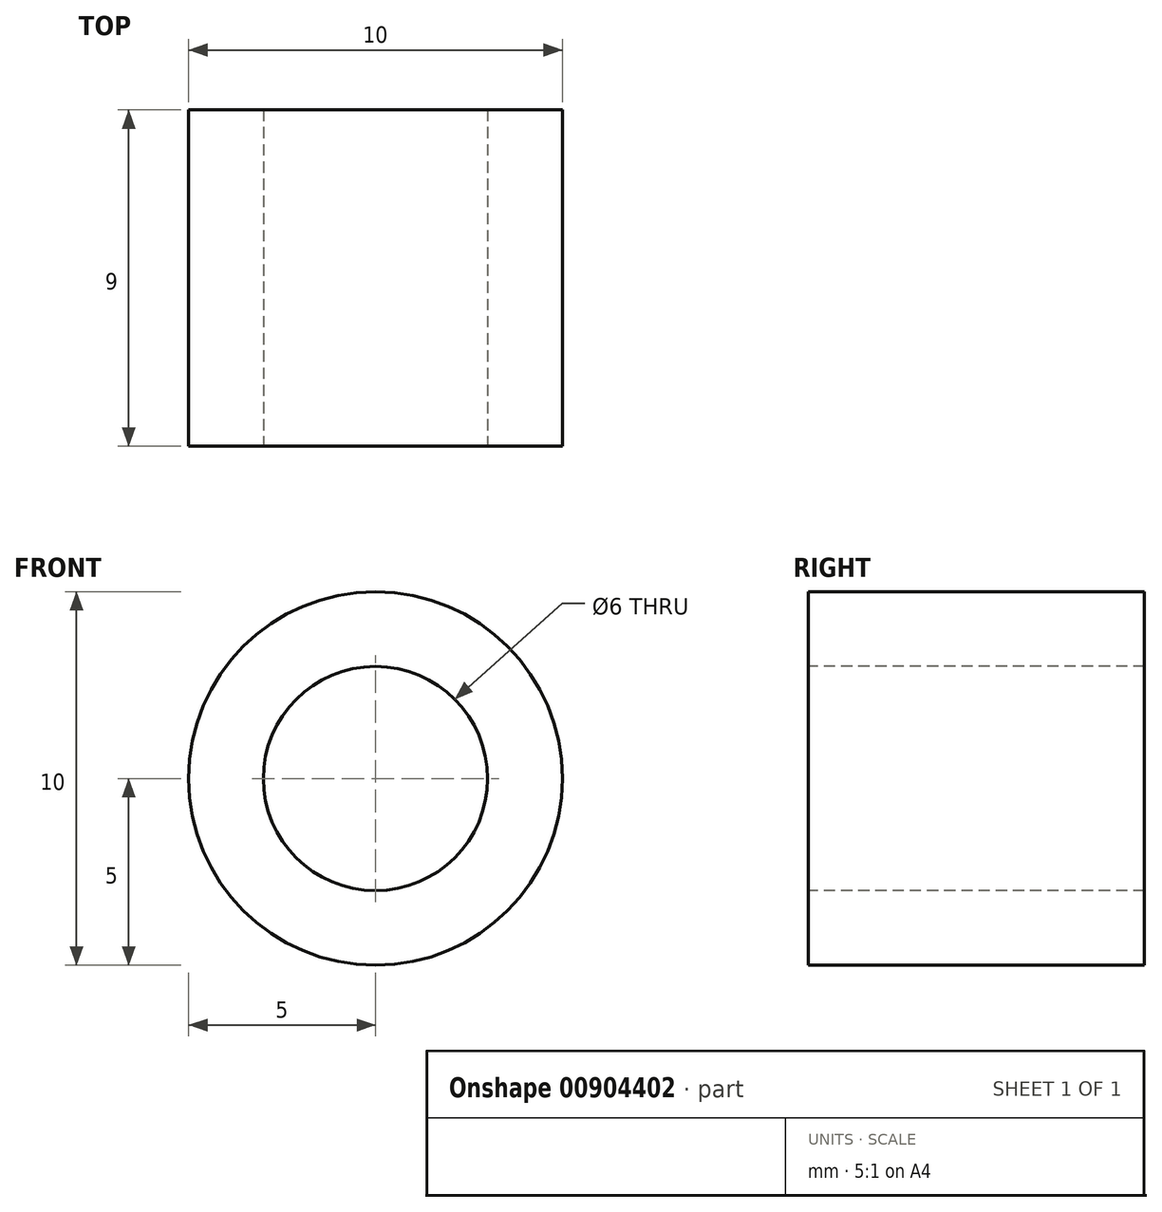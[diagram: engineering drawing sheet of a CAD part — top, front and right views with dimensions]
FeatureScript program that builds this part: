
annotation { "Feature Type Name" : "Feature", "Feature Type Description" : "" }
export const myFeature = defineFeature(function(context is Context, id is Id, definition is map)
    precondition{}
    {
        {
            var Q0;
            Q0=qCreatedBy(makeId("Front.planeOp"),FACE);
            var sketch = newSketch(context, id + "F0", { "sketchPlane" : qUnion([Q0])});
            skCircle(sketch, "E0", {"center": v(0, 0) * mm, "radius": 5 * mm});
            skCircle(sketch, "E1", {"center": v(0, 0) * mm, "radius": 3 * mm});
            skSolve(sketch);
        }
        {
            var Q0;
            Q0 = qSketchRegion(id + "F0", true);
            extrude(context, id + "F1", {"entities" : qUnion([Q0]), "oppositeDirection" : true, "depth" : 9 * mm, "offsetDistance" : 25 * mm});
        }
    });
